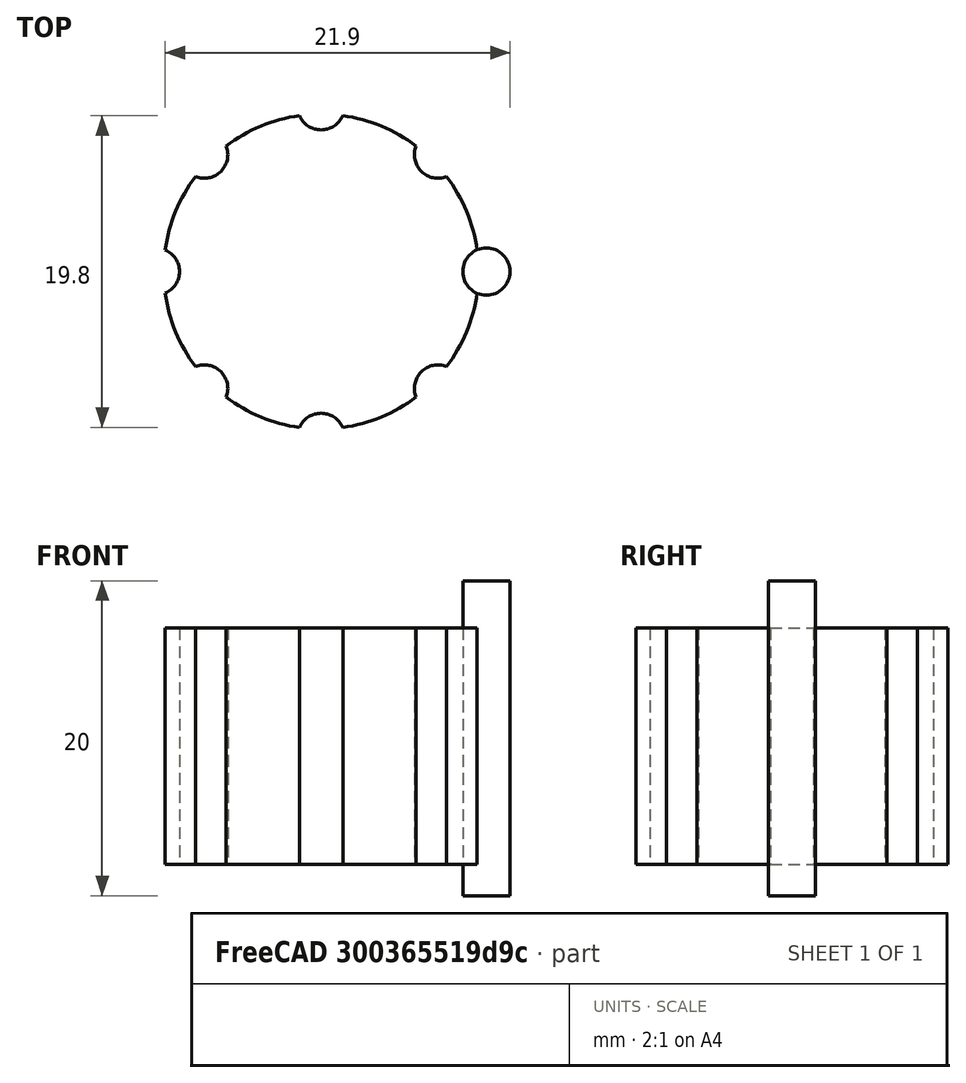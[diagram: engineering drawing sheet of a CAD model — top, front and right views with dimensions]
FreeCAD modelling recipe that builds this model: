
FCSTD DOCUMENT  (FreeCAD 1.0R39285 (Git))
Label: ojt1_t11r01_buttom
License: All rights reserved
objects: Part::Cylinder×2, Part::FeaturePython×1, Part::Cut×1
note: 3 computed .brp shape members not serialized (recipe doc carries the construction recipe); baked Part::Feature solids carry a one-line shape summary decoded from their .brp

FEATURE [Part::Cylinder] Cylinder  label="basis"
  Angle = 360
  AttacherType = Attacher::AttachEngine3D
  FirstAngle = 0
  Height = 15
  Radius = 10
  SecondAngle = 0
FEATURE [Part::Cylinder] Cylinder001  label="Cilindre001"
  Angle = 360
  AttacherType = Attacher::AttachEngine3D
  FirstAngle = 0
  Height = 20
  Placement = pos=(10.5,0,-2) rot=(0,0,1;0rad)
  Radius = 1.5
  SecondAngle = 0
FEATURE [Part::FeaturePython] Array  # Draft array (typed FeaturePython)
  AlwaysSyncPlacement = false
  Angle = 360
  ArrayType = 1
  Axis = (0,0,1)
  Base = -> Cylinder001
  Center = (0,0,1)
  Count = 8
  ExpandArray = false
  Fuse = false
  IntervalAxis = (0,0,0)
  IntervalX = (50,0,0)
  IntervalY = (0,50,0)
  IntervalZ = (0,0,50)
  NumberCircles = 3
  NumberPolar = 8
  NumberX = 2
  NumberY = 2
  NumberZ = 1
  PlacementList = 8 placements: [(10.5,0,-2),(7.42462,7.42462,-2),(0,10.5,-2),(-7.42462,7.42462,-2),(-10.5,1.28588e-15,-2),(-7.42462,-7.42462,-2),(-2.33147e-15,-10.5,-2),(7.42462,-7.42462,-2)]
  RadialDistance = 50
  ScaleList = (8) [(1,1,1),(1,1,1),(1,1,1),(1,1,1),(1,1,1),(1,1,1),(1,1,1),(1,1,1)]
  Symmetry = 1
  TangentialDistance = 25
FEATURE [Part::Cut] Cut  label="buttom"
  Base = -> Cylinder
  Refine = true
  Tool = -> Array
